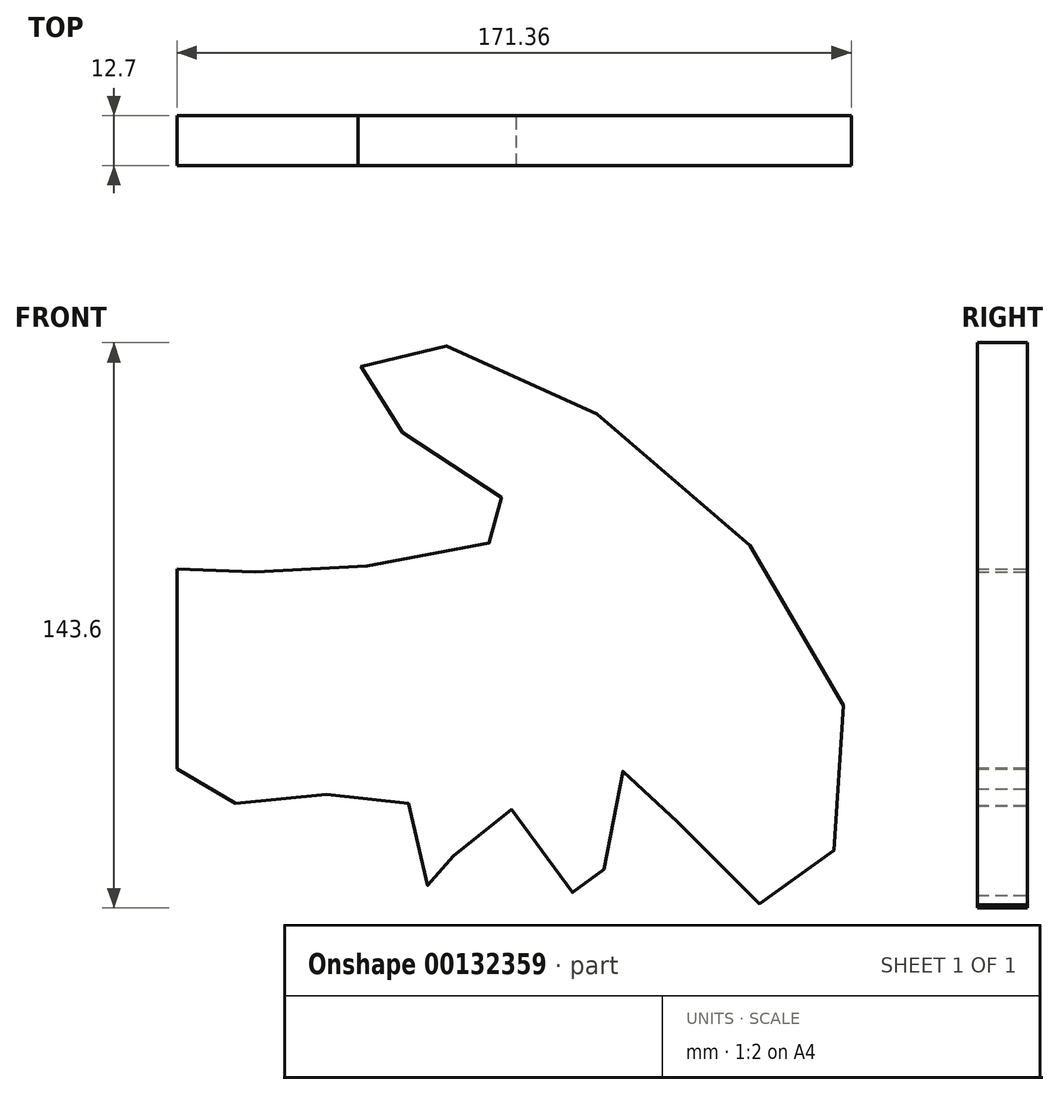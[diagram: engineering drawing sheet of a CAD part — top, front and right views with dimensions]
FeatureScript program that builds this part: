
annotation { "Feature Type Name" : "Feature", "Feature Type Description" : "" }
export const myFeature = defineFeature(function(context is Context, id is Id, definition is map)
    precondition{}
    {
        {
            var Q0;
            Q0=qCreatedBy(makeId("Front.planeOp"),FACE);
            var sketch = newSketch(context, id + "F0", { "sketchPlane" : qUnion([Q0])});
            skLineSegment(sketch, "E0", {"start": v(0, 0) * mm, "end": v(0, -50.8) * mm});
            skFitSpline(sketch, "E1", {"points": [v(0, -50.8) * mm, v(21.35, -60.11) * mm, v(58.78, -59.41) * mm, v(64.79, -82.89) * mm, v(81.78, -59.96) * mm, v(105.15, -86.01) * mm, v(113.89, -50.8) * mm, v(146.92, -84.67) * mm, v(169.87, -36.73) * mm, v(61.52, 57.54) * mm, v(46.99, 44.5) * mm, v(86.3, 13.17) * mm, v(38.3, 0) * mm, v(0, 0) * mm], "startDerivative": vector(306.15, -251.04) * mm, "endDerivative": vector(-422.94, 24.94) * mm});
            skSolve(sketch);
        }
        {
            var Q0;
            Q0=makeQuery(id+"F0.imprint","IMPRINT",FACE,{"disambiguationData":[TD([[makeQuery(id+"F0.imprint","IMPRINT",EDGE,{"derivedFrom":sQuery(id+"F0.wireOp",EDGE,"E0")}),1.0]])]});
            extrude(context, id + "F1", {"entities" : qUnion([Q0]), "depth" : 12.7 * mm});
        }
    });
